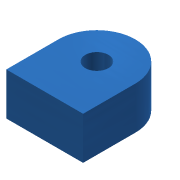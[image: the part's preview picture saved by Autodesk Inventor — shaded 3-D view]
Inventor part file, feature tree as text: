
AUTODESK INVENTOR PART (.ipt)
format: ipt  version: 2016 SP2 (Build 200236200, 236)  size: 108,032 bytes
history: native  units: mm
features: sketch x2, extrude x1, hole x1
ambient origin geometry x8: Origin, YZ Plane, XZ Plane, XY Plane, X Axis, Y Axis, Z Axis, Center Point
bodies: Solid1 (feature_tree)
feature tree (4):
  extrude  "Extrusion1"  Depth=49.0mm
  hole  "Hole1"  [1 undecoded]
  sketch  "Sketch1"  dims[d0=26.0mm d1=49.0mm]
  sketch  "Sketch2"  dims[d2=73.0mm d3=57.0mm d4=0.0mm d5=31.0mm d6=31.0mm d7=25.0mm d8=4.917mm d9=10.0mm d10=4.0mm d11=2.0mm d12=90.0deg d13=10.0mm d14=20.594885mm]
note: 1 required parameter value undecoded (feature->parameter linkage not recoverable at this tier; creation-order binding heuristic only, values carry confidence <= 0.55)
